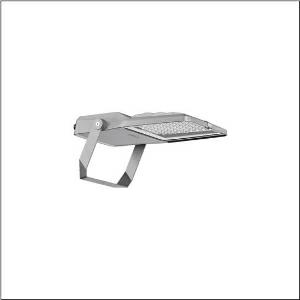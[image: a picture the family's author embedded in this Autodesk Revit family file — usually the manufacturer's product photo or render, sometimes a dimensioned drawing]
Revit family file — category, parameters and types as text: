
# Revit family: floodlight_fl_21_iq_mini___pl61_5xa7772d5c1a_2039
name_source: partatom
category: Lighting Fixtures
units: mm (PartAtom-declared; Revit-internal decimal feet)

## family parameters
Cut with Voids When Loaded = No
Host = Face
Light Source = No
Part Type = Normal
Room Calculation Point = No
Round Connector Dimension = Use Diameter
Shared = No

## types (1)
- --- (1 x LED, 16340 lm, 143 W, 4000K)
    Apparent Load = 143 VA
    CIE Flux Codes = 33 65 98 100 100
    Color Rendering = 80
    Color Temperature = 4000K
    Default Elevation = 1800 mm
    Description = Floodlight FL 21 iQ mini, floodlight, primary light control with lens, of PMMA, primary optical cover: protective disc, of toughened safety glass, transparent, light distribution: PL61, light emission: direct distribution, installation type: surface-mounted, lamps: LED, High Power LED, rated values: 16.340lm | 143W | 114,3lm/W (begin service life); end service life: 16.340lm | 151,6W; at 50% lumin. flux: 8.170lm | 60,6W | 134,8lm/W, colour temperature: 4000K, colour rendering: CRI > 80, light colour: 840, light setting 1 begin service life: 100% | 16.340lm | 143W | 114,3lm/W | 4.000K, light setting 1 end service life: 151,6W, further light settings possible, control: Street-Remote, Auto-Match, Temp-Guard, Night-Set, Smart-Wire, Desk-Remote (wireless, voltage-free reading and setting of iQ features in the workshop via application-optimized NFC function/RFID function), optimised constant luminous flux control (CLO 2.0), pre-setting: linear dimming characteristic, with terminal, 6-pole, mains connection: 220..240V, AC, 50/60Hz, luminaire housing, of diecast aluminium, powder-coated, SITECO metallic grey (DB 702S), corrosivity category C5 mid according to DIN EN ISO 12944suitable for swimming poolschlorine-resistant, sealing non-destructively replaceable, mounting bracket, of steel, galvanised, powder-coated, SITECO metallic grey (DB 702S), protection rating (complete): IP66, insulation class (complete): insulation class II (safety insulation), certification: CE, ENEC, VDE, protection symbol: D, impact resistance: IK08, permissible operating ambient temperature: -40..+40°C, permissible operating ambient temperature for outdoor applications: -40..+50°C, standard: DIN EN 12944, LABS conformity tested according to VDMA 24364:2018-05, packaging unit: 1 piece

Light Distribution: PL61
    Height = 70 mm
    Lamp = 1 x LED
    Lamp Light Flux = 16340 lm
    Lamp Power = 143 W
    Lamp count = 1
    Length = 485 mm
    Luminous efficacy = 114 lm/W
    Manufacturer = Siteco
    ModVariant = No
    Model = 5XA7772D5C1A
    Number of Poles = 1
    OnlyDefault = Yes
    Power Factor = 1
    Product Name = Floodlight FL 21 iQ mini | PL61
    Product group = floodlight | pylon annexe
    ProductGroupID = 6201
    Protection Class = Protection class II
    Protection Degree = IP 66
    RLX_Detail_Level = 1
    RLX_Emergency_Light_Flux = 0 lm
    RLX_Emergency_Type = 0
    RLX_Emergency_Type_DB = No
    RlxData = <blob elided: 96777 chars, md5=1240682c>
    Socket = socket
    Standby Power = 0 W
    System Light Flux = 16340 lm
    System Power = 143 W
    Type Comments = factory setting: luminous flux: 100 % | dim-lin: 254 | 730 mA
    Type Image = l_1006845.jpg
    URL = http://relux.com
    VarID = @adj_171747
    Voltage = 0 V
    Weight = 0.00 kg
    Width = 337 mm

## geometry (parser evidence)
native form markers: Blend x4, Sweep x11
no freeform markers — native parametric forms only
